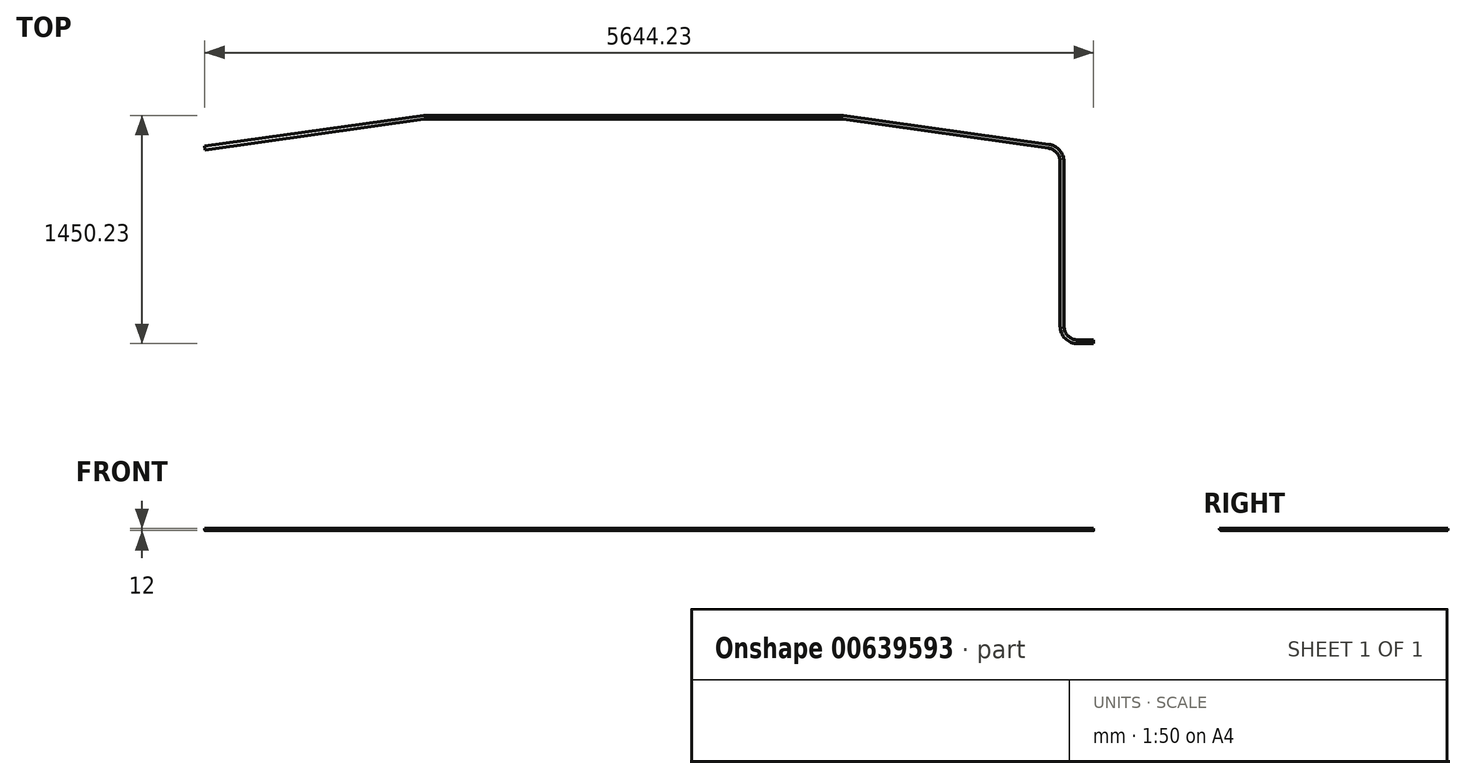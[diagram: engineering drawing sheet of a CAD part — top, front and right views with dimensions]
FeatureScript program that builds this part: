
annotation { "Feature Type Name" : "Feature", "Feature Type Description" : "" }
export const myFeature = defineFeature(function(context is Context, id is Id, definition is map)
    precondition{}
    {
        {
            var Q0;
            Q0=qCreatedBy(makeId("Top.planeOp"),FACE);
            var sketch = newSketch(context, id + "F0", { "sketchPlane" : qUnion([Q0])});
            skLineSegment(sketch, "E0", {"start": v(0, 0) * mm, "end": v(1389.35, 195.26) * mm});
            skLineSegment(sketch, "E1", {"start": v(1403.27, 196.23) * mm, "end": v(4039.29, 196.23) * mm});
            skLineSegment(sketch, "E2", {"start": v(4053.2, 195.26) * mm, "end": v(5356.47, 12.1) * mm});
            skLineSegment(sketch, "E3", {"start": v(5442.56, -86.93) * mm, "end": v(5442.56, -1130) * mm});
            skLineSegment(sketch, "E4", {"start": v(5542.56, -1230) * mm, "end": v(5642.56, -1230) * mm});
            skPoint(sketch, "E5.visualSharp", {"position": v(5442.56, -1230) * mm});
            skArc(sketch, "E5.filletArc", {"start": v(5442.56, -1130) * mm, "mid": v(5471.85, -1200.71) * mm, "end": v(5542.56, -1230) * mm});
            skPoint(sketch, "E6.visualSharp", {"position": v(5442.56, 0) * mm});
            skArc(sketch, "E6.filletArc", {"start": v(5442.56, -86.93) * mm, "mid": v(5418.03, -21.32) * mm, "end": v(5356.47, 12.1) * mm});
            skPoint(sketch, "E7.visualSharp", {"position": v(4046.28, 196.23) * mm});
            skArc(sketch, "E7.filletArc", {"start": v(4053.2, 195.26) * mm, "mid": v(4046.26, 196) * mm, "end": v(4039.29, 196.23) * mm});
            skPoint(sketch, "E8.visualSharp", {"position": v(1396.28, 196.23) * mm});
            skArc(sketch, "E8.filletArc", {"start": v(1403.27, 196.23) * mm, "mid": v(1396.3, 196) * mm, "end": v(1389.35, 195.26) * mm});
            skSolve(sketch);
        }
        {
            var Q0;
            Q0=sQuery(id+"F0.wireOp",EDGE,"E4");
            var Q1;
            Q1=sQuery(id+"F0.wireOp",VERTEX,"E4.end");
            cPlane(context, id + "F1", {"entities" : qUnion([Q0, Q1]), "cplaneType" : CPlaneType.LINE_POINT, "offset" : 25 * mm, "width" : 150 * mm, "height" : 150 * mm});
        }
        {
            var Q0;
            Q0=qCreatedBy(id+"F1.planeOp",FACE);
            var sketch = newSketch(context, id + "F2", { "sketchPlane" : qUnion([Q0])});
            skLineSegment(sketch, "E9.bottom", {"start": v(-1242, 0) * mm, "end": v(-1218, 0) * mm});
            skLineSegment(sketch, "E9.top", {"start": v(-1242, -12) * mm, "end": v(-1218, -12) * mm});
            skLineSegment(sketch, "E9.left", {"start": v(-1242, 0) * mm, "end": v(-1242, -12) * mm});
            skLineSegment(sketch, "E9.right", {"start": v(-1218, 0) * mm, "end": v(-1218, -12) * mm});
            skSolve(sketch);
        }
        {
            var Q0;
            Q0=makeQuery(id+"F2.imprint","IMPRINT",FACE,{"disambiguationData":[TD([[makeQuery(id+"F2.imprint","IMPRINT",EDGE,{"derivedFrom":sQuery(id+"F2.wireOp",EDGE,"E9.bottom")}),-1.0]])]});
            var Q1;
            Q1=sQuery(id+"F0.wireOp",EDGE,"E4");
            var Q2;
            Q2=sQuery(id+"F0.wireOp",EDGE,"E5.filletArc");
            var Q3;
            Q3=sQuery(id+"F0.wireOp",EDGE,"E3");
            var Q4;
            Q4=sQuery(id+"F0.wireOp",EDGE,"E6.filletArc");
            var Q5;
            Q5=sQuery(id+"F0.wireOp",EDGE,"E2");
            var Q6;
            Q6=sQuery(id+"F0.wireOp",EDGE,"E7.filletArc");
            var Q7;
            Q7=sQuery(id+"F0.wireOp",EDGE,"E1");
            var Q8;
            Q8=sQuery(id+"F0.wireOp",EDGE,"E8.filletArc");
            var Q9;
            Q9=sQuery(id+"F0.wireOp",EDGE,"E0");
            sweep(context, id + "F3", {"profiles" : qUnion([Q0]), "path" : qUnion([Q1, Q2, Q3, Q4, Q5, Q6, Q7, Q8, Q9])});
        }
        {
            var Q0;
            Q0=makeQuery(id+"F3.opSweep","SWEPT_EDGE",EDGE,{"disambiguationData":[OSD([sQuery(id+"F0.wireOp",EDGE,"E4"),sQuery(id+"F2.wireOp",EDGE,"E9.top"),sQuery(id+"F2.wireOp",EDGE,"E9.right")])]});
            fillet(context, id + "F4", {"entities" : qUnion([Q0]), "radius" : 5 * mm, "tangentPropagation" : true, "allowEdgeOverflow" : false});
        }
        {
            var Q0;
            Q0=makeQuery(id+"F3.opSweep","SWEPT_EDGE",EDGE,{"disambiguationData":[OSD([sQuery(id+"F0.wireOp",EDGE,"E4"),sQuery(id+"F2.wireOp",EDGE,"E9.top"),sQuery(id+"F2.wireOp",EDGE,"E9.left")])]});
            fillet(context, id + "F5", {"entities" : qUnion([Q0]), "radius" : 12 * mm, "tangentPropagation" : true, "allowEdgeOverflow" : false});
        }
    });
